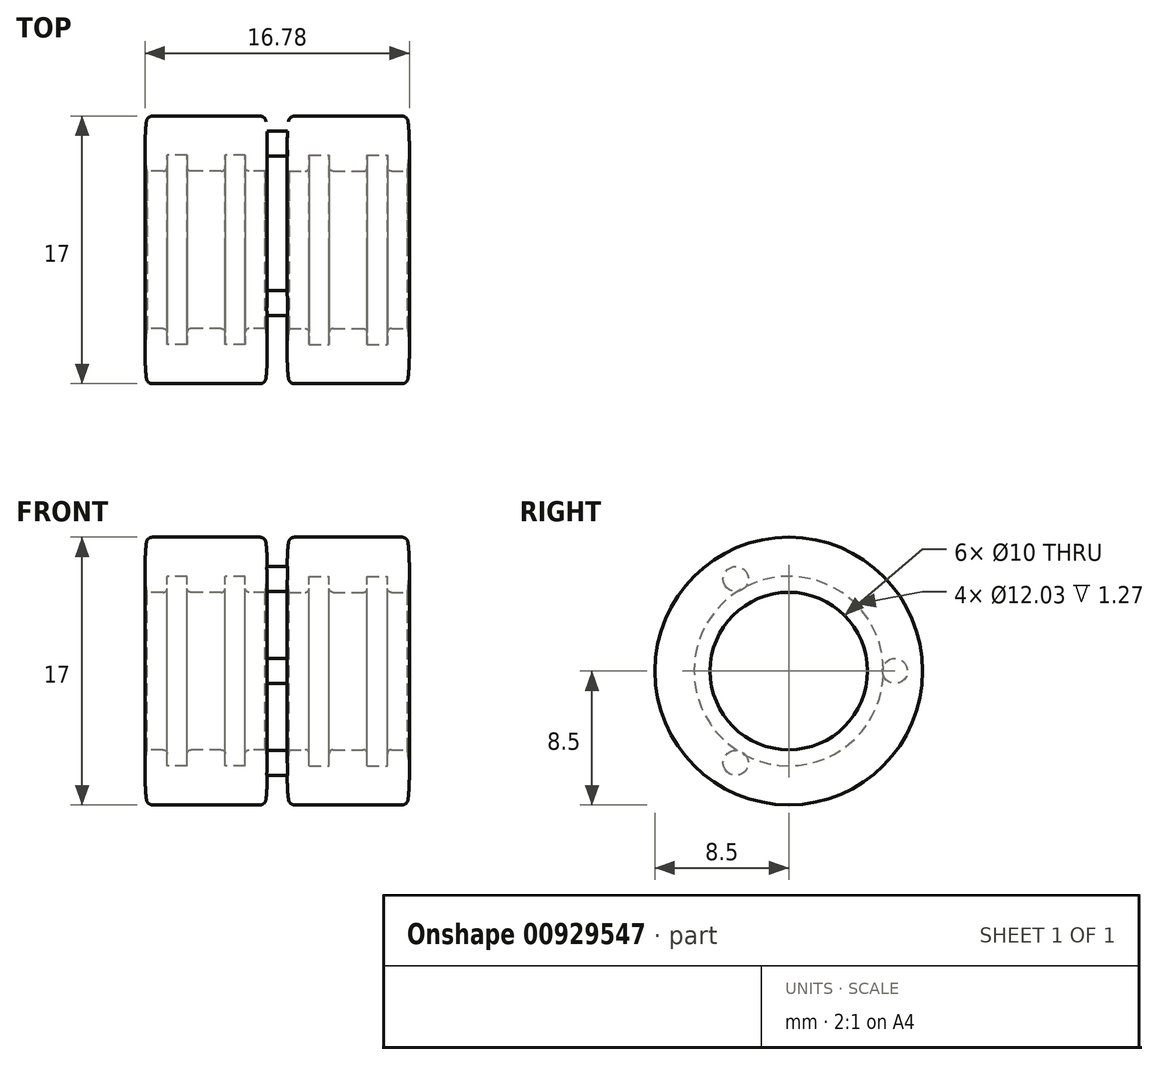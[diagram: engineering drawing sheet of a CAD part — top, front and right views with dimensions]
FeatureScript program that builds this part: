
annotation { "Feature Type Name" : "Feature", "Feature Type Description" : "" }
export const myFeature = defineFeature(function(context is Context, id is Id, definition is map)
    precondition{}
    {
        {
            var Q0;
            Q0=qCreatedBy(makeId("Front.planeOp"),FACE);
            var sketch = newSketch(context, id + "F0", { "sketchPlane" : qUnion([Q0])});
            skLineSegment(sketch, "E0", {"start": v(0, 0) * mm, "end": v(0, 5) * mm, "construction": true});
            skLineSegment(sketch, "E1.bottom", {"start": v(-3.75, 8.5) * mm, "end": v(3.75, 8.5) * mm});
            skLineSegment(sketch, "E1.top", {"start": v(-3.75, 5) * mm, "end": v(-2.48, 5) * mm});
            skLineSegment(sketch, "E2", {"start": v(0, 0) * mm, "end": v(-9.59, 0) * mm, "construction": true});
            skArc(sketch, "E3", {"start": v(-3.75, 8.5) * mm, "mid": v(-3.88, 6.75) * mm, "end": v(-3.75, 5) * mm});
            skArc(sketch, "E4", {"start": v(3.75, 5) * mm, "mid": v(3.88, 6.75) * mm, "end": v(3.75, 8.5) * mm});
            skLineSegment(sketch, "E5.top", {"start": v(-2.48, 6.02) * mm, "end": v(-1.2, 6.02) * mm});
            skLineSegment(sketch, "E5.left", {"start": v(-2.48, 5) * mm, "end": v(-2.48, 6.02) * mm});
            skLineSegment(sketch, "E5.right", {"start": v(-1.2, 5) * mm, "end": v(-1.2, 6.02) * mm});
            skLineSegment(sketch, "E6.top", {"start": v(1.2, 6.02) * mm, "end": v(2.48, 6.02) * mm});
            skLineSegment(sketch, "E6.left", {"start": v(1.2, 5) * mm, "end": v(1.2, 6.02) * mm});
            skLineSegment(sketch, "E6.right", {"start": v(2.48, 5) * mm, "end": v(2.48, 6.02) * mm});
            skLineSegment(sketch, "E7.trimOffspring", {"start": v(-1.2, 5) * mm, "end": v(0, 5) * mm});
            skLineSegment(sketch, "E8.trimOffspring", {"start": v(2.48, 5) * mm, "end": v(3.75, 5) * mm});
            skLineSegment(sketch, "E9", {"start": v(0, 5) * mm, "end": v(1.2, 5) * mm});
            skSolve(sketch);
        }
        {
            var Q0;
            Q0 = qSketchRegion(id + "F0", true);
            var Q1;
            Q1=sQuery(id+"F0.wireOp",EDGE,"E2");
            revolve(context, id + "F1", {"surfaceOperationType" : NewSurfaceOperationType.NEW, "entities" : qUnion([Q0]), "axis" : qUnion([Q1]), "revolveType" : RevolveType.FULL});
        }
        {
            var Q0;
            Q0=makeQuery(id+"F1.opRevolve","SWEPT_EDGE",EDGE,{"disambiguationData":[OSD([sQuery(id+"F0.wireOp",EDGE,"E1.bottom"),sQuery(id+"F0.wireOp",EDGE,"E3")])]});
            var Q1;
            Q1=makeQuery(id+"F1.opRevolve","SWEPT_EDGE",EDGE,{"disambiguationData":[OSD([sQuery(id+"F0.wireOp",EDGE,"E1.bottom"),sQuery(id+"F0.wireOp",EDGE,"E4")])]});
            fillet(context, id + "F2", {"entities" : qUnion([Q0, Q1]), "radius" : 0.38 * mm, "tangentPropagation" : true, "allowEdgeOverflow" : false});
        }
        {
            var Q0;
            Q0=makeQuery(id+"F1.opRevolve","SWEPT_FACE",FACE,{"disambiguationData":[OSD([sQuery(id+"F0.wireOp",EDGE,"E5.left")])]});
            var sketch = newSketch(context, id + "F3", { "sketchPlane" : qUnion([Q0])});
            skCircle(sketch, "E10", {"center": v(6.74, 0) * mm, "radius": 0.8 * mm});
            skCircle(sketch, "E11", {"center": v(-3.37, 5.84) * mm, "radius": 0.8 * mm});
            skCircle(sketch, "E12", {"center": v(-3.37, -5.84) * mm, "radius": 0.8 * mm});
            skCircle(sketch, "E13", {"center": v(0, 0) * mm, "radius": 6.74 * mm, "construction": true});
            skLineSegment(sketch, "E14", {"start": v(-3.37, 5.84) * mm, "end": v(-3.37, -5.84) * mm, "construction": true});
            skLineSegment(sketch, "E15", {"start": v(-3.37, 5.84) * mm, "end": v(6.74, 0) * mm, "construction": true});
            skLineSegment(sketch, "E16", {"start": v(6.74, 0) * mm, "end": v(-3.37, -5.84) * mm, "construction": true});
            skSolve(sketch);
        }
        {
            var Q0;
            Q0 = qSketchRegion(id + "F3", true);
            extrude(context, id + "F4", {"entities" : qUnion([Q0]), "operationType" : NewBodyOperationType.ADD, "oppositeDirection" : true, "depth" : 2.03 * mm, "offsetDistance" : 25.4 * mm});
        }
        {
            var Q0;
            Q0=makeQuery(id+"F1.opRevolve","SWEPT_EDGE",EDGE,{"disambiguationData":[OSD([sQuery(id+"F0.wireOp",EDGE,"E1.top"),sQuery(id+"F0.wireOp",EDGE,"E5.left")])]});
            var Q1;
            Q1=makeQuery(id+"F1.opRevolve","SWEPT_EDGE",EDGE,{"disambiguationData":[OSD([sQuery(id+"F0.wireOp",EDGE,"E5.right"),sQuery(id+"F0.wireOp",EDGE,"E7.trimOffspring")])]});
            var Q2;
            Q2=makeQuery(id+"F1.opRevolve","SWEPT_EDGE",EDGE,{"disambiguationData":[OSD([sQuery(id+"F0.wireOp",EDGE,"E6.left"),sQuery(id+"F0.wireOp",EDGE,"E9")])]});
            var Q3;
            Q3=makeQuery(id+"F1.opRevolve","SWEPT_EDGE",EDGE,{"disambiguationData":[OSD([sQuery(id+"F0.wireOp",EDGE,"E6.right"),sQuery(id+"F0.wireOp",EDGE,"E8.trimOffspring")])]});
            fillet(context, id + "F5", {"entities" : qUnion([Q0, Q1, Q2, Q3]), "radius" : 0.25 * mm, "tangentPropagation" : true, "allowEdgeOverflow" : false});
        }
        {
            var Q0;
            Q0=makeQuery(id+"F1.opRevolve","SWEPT_BODY",BODY,{"disambiguationData":[OSD([sQuery(id+"F0.wireOp",EDGE,"E1.bottom"),sQuery(id+"F0.wireOp",EDGE,"E1.top"),sQuery(id+"F0.wireOp",EDGE,"E3"),sQuery(id+"F0.wireOp",EDGE,"E4"),sQuery(id+"F0.wireOp",EDGE,"E5.top"),sQuery(id+"F0.wireOp",EDGE,"E5.left"),sQuery(id+"F0.wireOp",EDGE,"E5.right"),sQuery(id+"F0.wireOp",EDGE,"E6.top"),sQuery(id+"F0.wireOp",EDGE,"E6.left"),sQuery(id+"F0.wireOp",EDGE,"E6.right"),sQuery(id+"F0.wireOp",EDGE,"E7.trimOffspring"),sQuery(id+"F0.wireOp",EDGE,"E8.trimOffspring"),sQuery(id+"F0.wireOp",EDGE,"E9")])]});
            var Q1;
            Q1=makeQuery(id+"F4.opExtrude","CAP_FACE",FACE,{"disambiguationData":[OSD([sQuery(id+"F3.wireOp",EDGE,"E10")])],"isStart":false});
            mirror(context, id + "F6", {"operationType" : NewBodyOperationType.ADD, "entities" : qUnion([Q0]), "mirrorPlane" : qUnion([Q1])});
        }
    });
